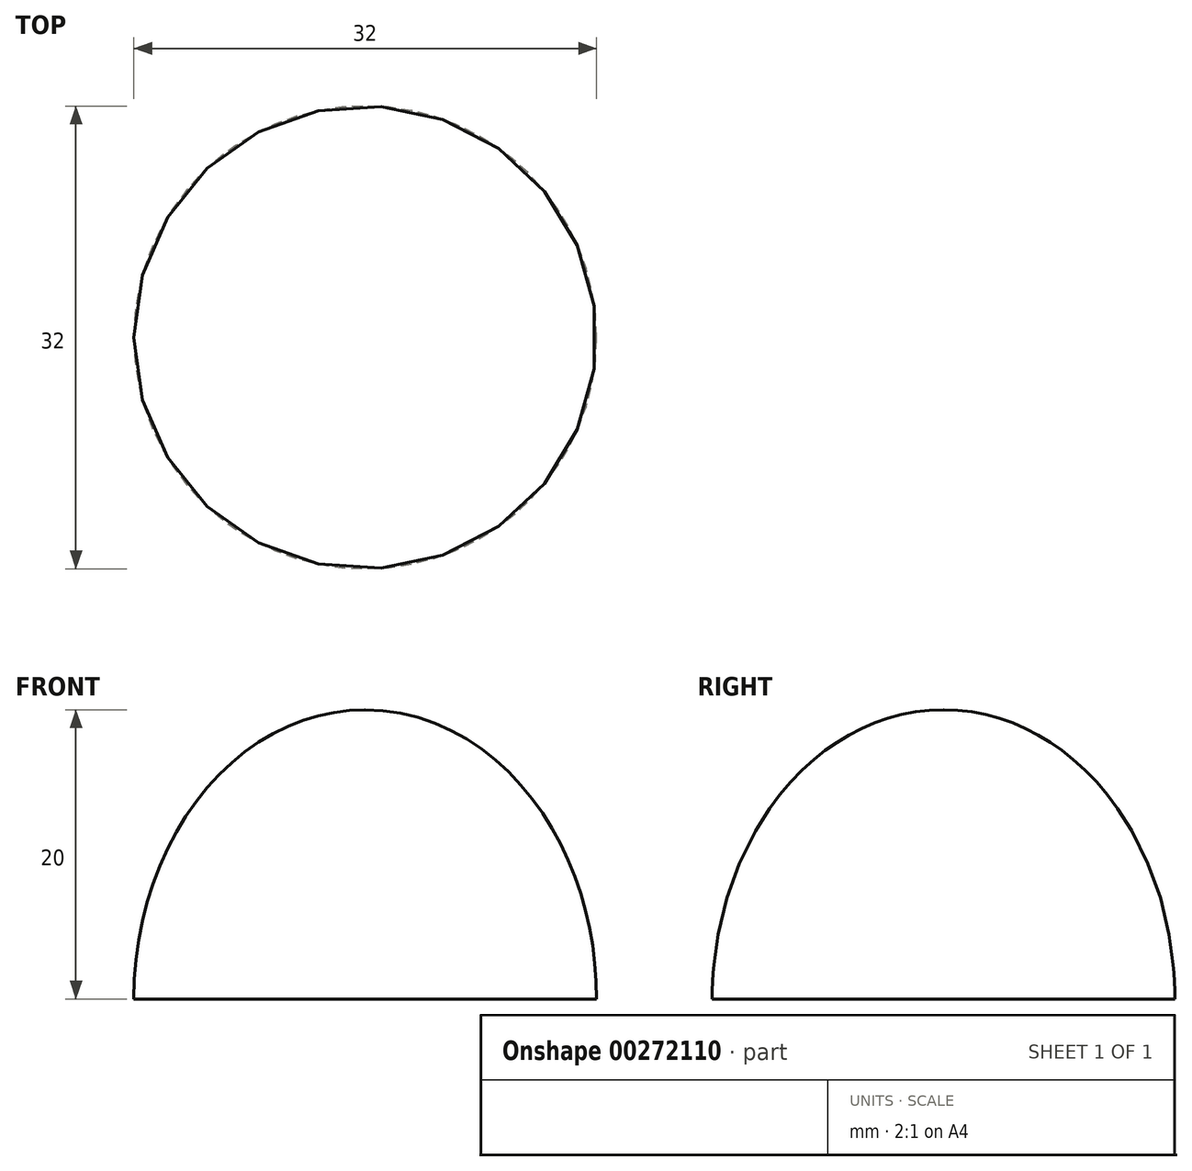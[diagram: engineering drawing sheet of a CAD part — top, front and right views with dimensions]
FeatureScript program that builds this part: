
annotation { "Feature Type Name" : "Feature", "Feature Type Description" : "" }
export const myFeature = defineFeature(function(context is Context, id is Id, definition is map)
    precondition{}
    {
        {
            var Q0;
            Q0=qCreatedBy(makeId("Front.planeOp"),FACE);
            var sketch = newSketch(context, id + "F0", { "sketchPlane" : qUnion([Q0])});
            skEllipticalArc(sketch, "E0", {});
            skLineSegment(sketch, "E1", {"start": v(-16, 0) * mm, "end": v(0, 0) * mm});
            skLineSegment(sketch, "E2", {"start": v(0, 20) * mm, "end": v(0, 0) * mm});
            const initialGuessF0  = {"E0": [0, 0, -1, 0, 0.016, 0.02, 4.71238898038469, 6.283185307179586]};
            skSetInitialGuess(sketch, initialGuessF0);
            skSolve(sketch);
        }
        {
            var Q0;
            Q0=makeQuery(id+"F0.imprint","IMPRINT",FACE,{"disambiguationData":[TD([[makeQuery(id+"F0.imprint","IMPRINT",EDGE,{"derivedFrom":sQuery(id+"F0.wireOp",EDGE,"E0")}),1.0]])]});
            var Q1;
            Q1=sQuery(id+"F0.wireOp",EDGE,"E2");
            revolve(context, id + "F1", {"entities" : qUnion([Q0]), "axis" : qUnion([Q1]), "revolveType" : RevolveType.FULL});
        }
    });
